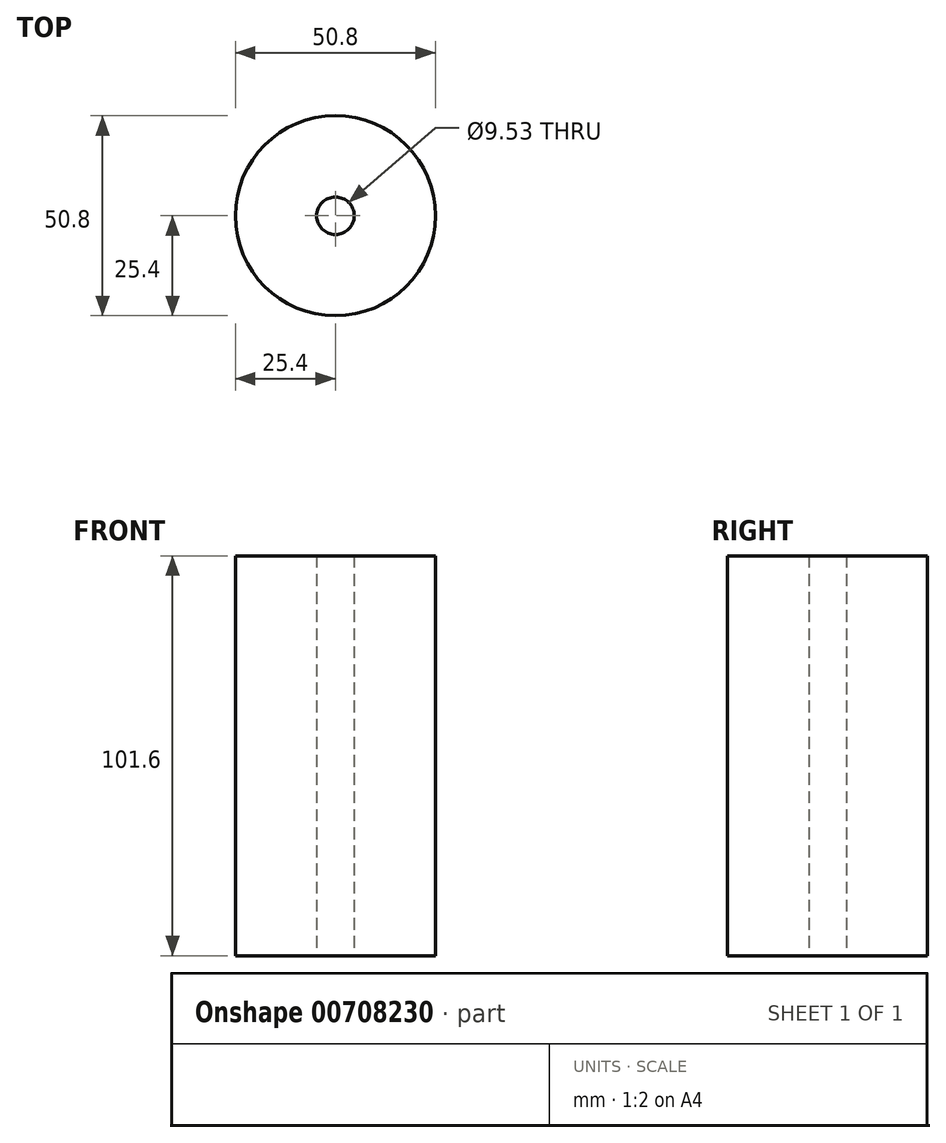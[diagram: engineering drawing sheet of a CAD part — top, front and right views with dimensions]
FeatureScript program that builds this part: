
annotation { "Feature Type Name" : "Feature", "Feature Type Description" : "" }
export const myFeature = defineFeature(function(context is Context, id is Id, definition is map)
    precondition{}
    {
        {
            var Q0;
            Q0=qCreatedBy(makeId("Top.planeOp"),FACE);
            var sketch = newSketch(context, id + "F0", { "sketchPlane" : qUnion([Q0])});
            skCircle(sketch, "E0", {"center": v(0, 0) * mm, "radius": 25.4 * mm});
            skCircle(sketch, "E1", {"center": v(0, 0) * mm, "radius": 4.76 * mm});
            skSolve(sketch);
        }
        {
            var Q0;
            Q0 = qSketchRegion(id + "F0", true);
            extrude(context, id + "F1", {"entities" : qUnion([Q0]), "depth" : 101.6 * mm, "offsetDistance" : 25.4 * mm});
        }
    });
